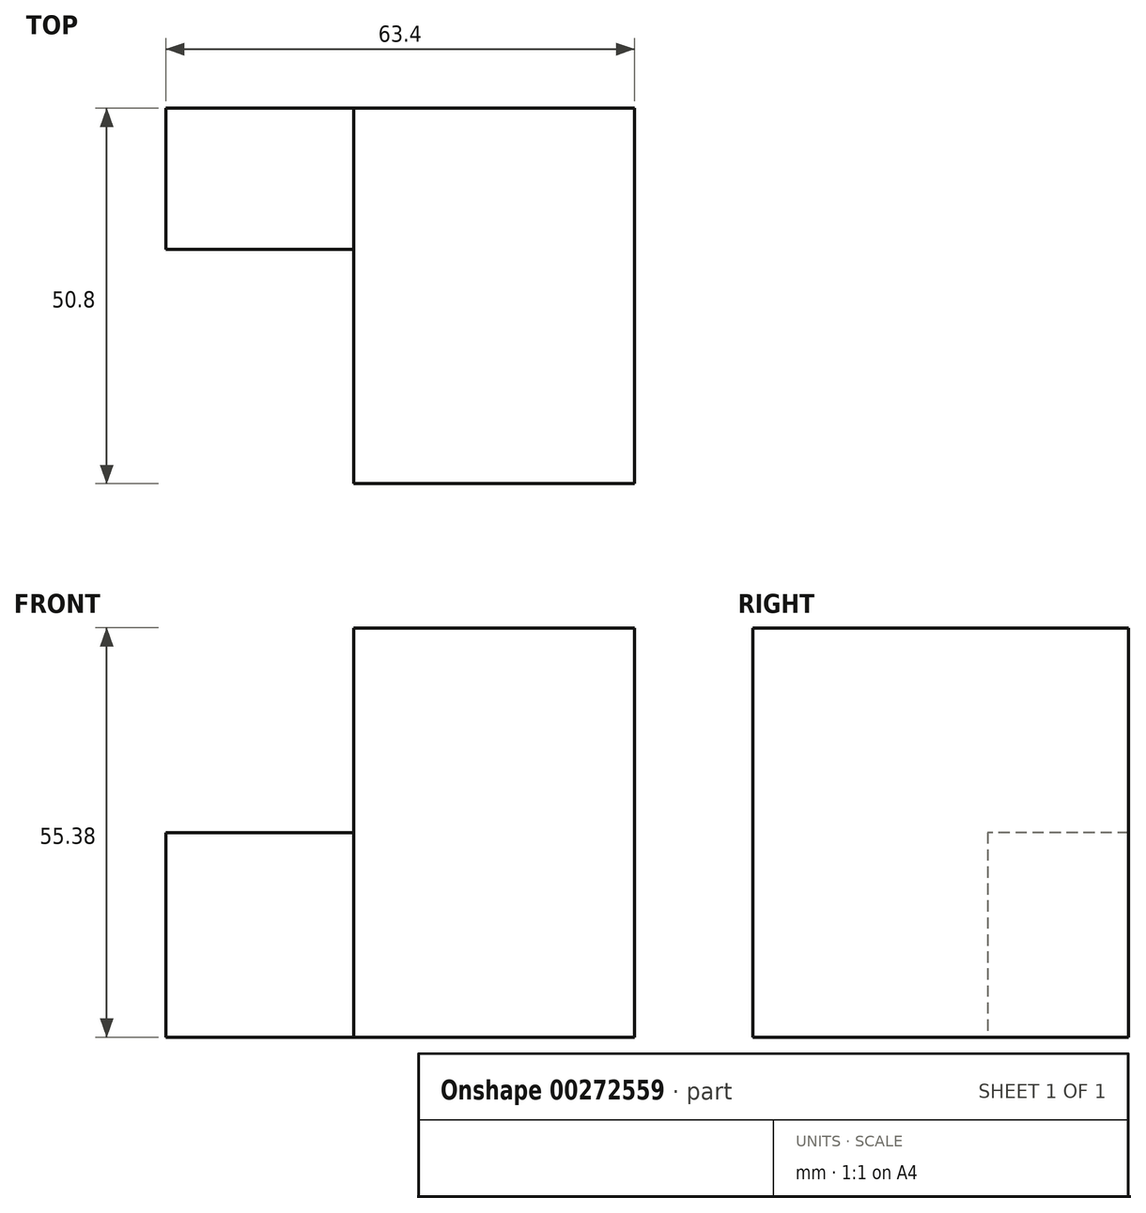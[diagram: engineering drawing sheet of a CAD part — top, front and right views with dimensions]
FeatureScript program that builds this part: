
annotation { "Feature Type Name" : "Feature", "Feature Type Description" : "" }
export const myFeature = defineFeature(function(context is Context, id is Id, definition is map)
    precondition{}
    {
        {
            var Q0;
            Q0=qCreatedBy(makeId("Front.planeOp"),FACE);
            var sketch = newSketch(context, id + "F0", { "sketchPlane" : qUnion([Q0])});
            skLineSegment(sketch, "E0", {"start": v(0, 55.38) * mm, "end": v(-38, 55.38) * mm});
            skLineSegment(sketch, "E1", {"start": v(-38, 55.38) * mm, "end": v(-38, 0) * mm});
            skLineSegment(sketch, "E2", {"start": v(-38, 0) * mm, "end": v(0, 0) * mm});
            skLineSegment(sketch, "E3", {"start": v(0, 0) * mm, "end": v(0, 55.38) * mm});
            skSolve(sketch);
        }
        {
            var Q0;
            Q0=makeQuery(id+"F0.imprint","IMPRINT",FACE,{"disambiguationData":[TD([[makeQuery(id+"F0.imprint","IMPRINT",EDGE,{"derivedFrom":sQuery(id+"F0.wireOp",EDGE,"E0")}),1.0]])]});
            extrude(context, id + "F1", {"entities" : qUnion([Q0]), "depth" : 50.8 * mm});
        }
        {
            var Q0;
            Q0=makeQuery(id+"F1.opExtrude","SWEPT_FACE",FACE,{"disambiguationData":[OSD([sQuery(id+"F0.wireOp",EDGE,"E1")])]});
            var sketch = newSketch(context, id + "F2", { "sketchPlane" : qUnion([Q0])});
            skLineSegment(sketch, "E4", {"start": v(0, 27.69) * mm, "end": v(19.1, 27.69) * mm});
            skLineSegment(sketch, "E5", {"start": v(19.1, 27.69) * mm, "end": v(19.1, 0) * mm});
            skLineSegment(sketch, "E6", {"start": v(19.1, 0) * mm, "end": v(0, 0) * mm});
            skLineSegment(sketch, "E7", {"start": v(0, 0) * mm, "end": v(0, 27.69) * mm});
            skSolve(sketch);
        }
        {
            var Q0;
            Q0 = qSketchRegion(id + "F2", true);
            extrude(context, id + "F3", {"entities" : qUnion([Q0]), "operationType" : NewBodyOperationType.ADD, "depth" : 25.4 * mm});
        }
    });
